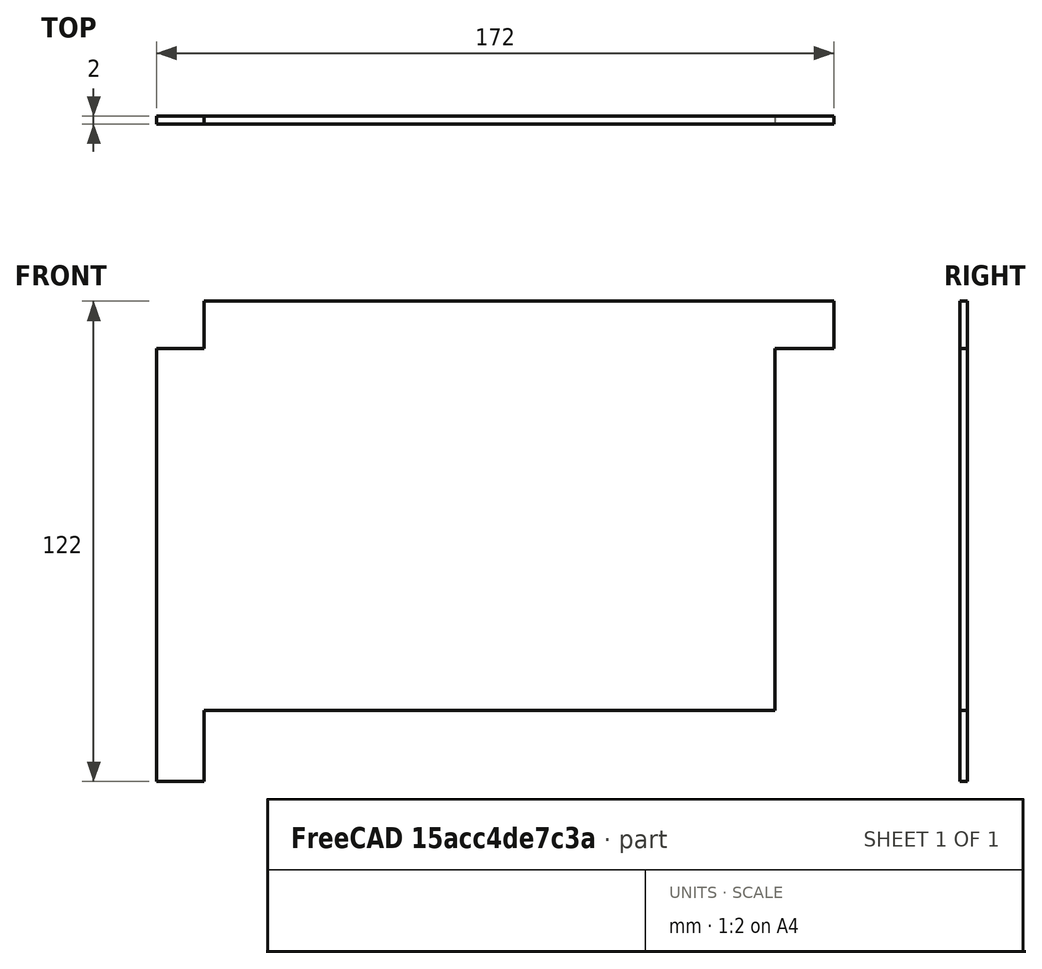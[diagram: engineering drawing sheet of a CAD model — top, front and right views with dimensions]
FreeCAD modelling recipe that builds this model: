
FCSTD DOCUMENT  (FreeCAD 0.20R29177 (Git))
Label: 8000_Profile_Template_Plexi
License: All rights reserved
LicenseURL: http://en.wikipedia.org/wiki/All_rights_reserved
objects: TechDraw::DrawViewDimension×6, Sketcher::SketchObject×1, PartDesign::Pad×1, PartDesign::Body×1, TechDraw::DrawSVGTemplate×1, TechDraw::DrawViewPart×1, TechDraw::DrawPage×1
note: 4 computed .brp shape members not serialized (recipe doc carries the construction recipe); baked Part::Feature solids carry a one-line shape summary decoded from their .brp

FEATURE [Sketcher::SketchObject] Sketch
  FullyConstrained = true
  MapMode = 5
  Placement = pos=(0,0,0) rot=(1,0,0;1.5708rad)
  Support = -> [XZ_Plane]
  sketch-geometry (10):
    g0: LineSegment StartX=0 StartY=0 StartZ=0 EndX=0 EndY=110 EndZ=0
    g1: LineSegment StartX=0 StartY=0 StartZ=0 EndX=12 EndY=0 EndZ=0
    g2: LineSegment StartX=12 StartY=0 StartZ=0 EndX=12 EndY=18 EndZ=0
    g3: LineSegment StartX=12 StartY=18 StartZ=0 EndX=157 EndY=18 EndZ=0
    g4: LineSegment StartX=157 StartY=18 StartZ=0 EndX=157 EndY=110 EndZ=0
    g5: LineSegment StartX=157 StartY=110 StartZ=0 EndX=172 EndY=110 EndZ=0
    g6: LineSegment StartX=172 StartY=110 StartZ=0 EndX=172 EndY=122 EndZ=0
    g7: LineSegment StartX=172 StartY=122 StartZ=0 EndX=12 EndY=122 EndZ=0
    g8: LineSegment StartX=0 StartY=110 StartZ=0 EndX=12 EndY=110 EndZ=0
    g9: LineSegment StartX=12 StartY=110 StartZ=0 EndX=12 EndY=122 EndZ=0
  constraints (30):
    c: Vertical(g0)
    c: DistanceY(g0,g0) = 110
    c: Coincident(g1,g0)
    c: Horizontal(g1)
    c: Coincident(g2,g1)
    c: Vertical(g2)
    c: Coincident(g3,g2)
    c: Horizontal(g3)
    c: Coincident(g4,g3)
    c: Vertical(g4)
    c: Coincident(g5,g4)
    c: Horizontal(g5)
    c: Coincident(g6,g5)
    c: Vertical(g6)
    c: Horizontal(g7)
    c: DistanceX(g0,g1) = 12
    c: DistanceY(g3,g4) = 92
    c: DistanceY(g1,g2) = 18
    c: Coincident(g8,g0)
    c: Horizontal(g8)
    c: Coincident(g9,g8)
    c: Coincident(g9,g7)
    c: Vertical(g9)
    c: DistanceY(g6,g6) = 12
    c: Equal(g1,g8)
    c: Horizontal(g4,g8)
    c: DistanceX(g2,g3) = 145
    c: DistanceX(g7,g6) = 160
    c: Coincident(g6,g7)
    c: Coincident(g-1,g0)
FEATURE [PartDesign::Pad] Pad
  Direction = (0,-1,-2e-16)
  Length = 2
  Length2 = 100
  Placement = pos=(0,0,0) rot=(1,0,0;1.5708rad)
  Profile = -> Sketch
  Type = 0
FEATURE [PartDesign::Body] Body
  Group = -> [Sketch,Pad]
  Origin = -> Origin
  Tip = -> Pad
FEATURE [TechDraw::DrawSVGTemplate] Template
  EditableTexts = Designed_by_Name=RIP; Drawing_number=8000_Profile_Template; FC-Date=Date; FC-SC=1:1; FC-SH=Sheet; FC-Title=Keyboard Template; Subtitle=Printable; Weight=-
  Height = 210
  Orientation = 1
  Width = 297
FEATURE [TechDraw::DrawViewPart] View
  CoarseView = false
  Direction = (0,-1,0)
  Focus = 100
  HardHidden = false
  IsoCount = 0
  IsoHidden = false
  IsoVisible = false
  LockPosition = false
  Perspective = false
  Rotation = 0
  ScaleType = 0
  SeamHidden = false
  SeamVisible = true
  SmoothHidden = false
  SmoothVisible = true
  Source = -> [Template,Pad]
  X = 125.167
  XDirection = (0.866,0.5,0)
  Y = 122.642
FEATURE [TechDraw::DrawViewDimension] Dimension
  AngleOverride = false
  Arbitrary = false
  ArbitraryTolerances = false
  EqualTolerance = true
  ExtensionAngle = 0
  FormatSpec = %.2f
  FormatSpecOverTolerance = %+.2f
  FormatSpecUnderTolerance = %+.2f
  Inverted = false
  LineAngle = 0
  LockPosition = false
  MeasureType = 1
  OverTolerance = 0
  References2D = -> [View]
  Rotation = 0
  ScaleType = 0
  TheoreticalExact = false
  Type = 2
  UnderTolerance = 0
  X = 109.768
  Y = 55
FEATURE [TechDraw::DrawViewDimension] Dimension001
  AngleOverride = false
  Arbitrary = false
  ArbitraryTolerances = false
  EqualTolerance = true
  ExtensionAngle = 0
  FormatSpec = %.2f
  FormatSpecOverTolerance = %+.2f
  FormatSpecUnderTolerance = %+.2f
  Inverted = false
  LineAngle = 0
  LockPosition = false
  MeasureType = 1
  OverTolerance = 0
  References2D = -> [View]
  Rotation = 0
  ScaleType = 0
  TheoreticalExact = false
  Type = 2
  UnderTolerance = 0
  X = 95.3726
  Y = 3.43089
FEATURE [TechDraw::DrawViewDimension] Dimension003
  AngleOverride = false
  Arbitrary = false
  ArbitraryTolerances = false
  EqualTolerance = true
  ExtensionAngle = 0
  FormatSpec = %.2f
  FormatSpecOverTolerance = %+.2f
  FormatSpecUnderTolerance = %+.2f
  Inverted = false
  LineAngle = 0
  LockPosition = false
  MeasureType = 1
  OverTolerance = 0
  References2D = -> [View]
  Rotation = 0
  ScaleType = 0
  TheoreticalExact = false
  Type = 1
  UnderTolerance = 0
  X = -82.4267
  Y = -79.7805
FEATURE [TechDraw::DrawViewDimension] Dimension004
  AngleOverride = false
  Arbitrary = false
  ArbitraryTolerances = false
  EqualTolerance = true
  ExtensionAngle = 0
  FormatSpec = %.2f
  FormatSpecOverTolerance = %+.2f
  FormatSpecUnderTolerance = %+.2f
  Inverted = false
  LineAngle = 0
  LockPosition = false
  MeasureType = 1
  OverTolerance = 0
  References2D = -> [View]
  Rotation = 0
  ScaleType = 0
  TheoreticalExact = false
  Type = 2
  UnderTolerance = 0
  X = -105.784
  Y = -3.15447
FEATURE [TechDraw::DrawViewDimension] Dimension005
  AngleOverride = false
  Arbitrary = false
  ArbitraryTolerances = false
  EqualTolerance = true
  ExtensionAngle = 0
  FormatSpec = %.2f
  FormatSpecOverTolerance = %+.2f
  FormatSpecUnderTolerance = %+.2f
  Inverted = false
  LineAngle = 0
  LockPosition = false
  MeasureType = 1
  OverTolerance = 0
  References2D = -> [View]
  Rotation = 0
  ScaleType = 0
  TheoreticalExact = false
  Type = 1
  UnderTolerance = 0
  X = -10.0189
  Y = -45.8374
FEATURE [TechDraw::DrawViewDimension] Dimension006
  AngleOverride = false
  Arbitrary = false
  ArbitraryTolerances = false
  EqualTolerance = true
  ExtensionAngle = 0
  FormatSpec = %.2f
  FormatSpecOverTolerance = %+.2f
  FormatSpecUnderTolerance = %+.2f
  Inverted = false
  LineAngle = 0
  LockPosition = false
  MeasureType = 1
  OverTolerance = 0
  References2D = -> [View]
  Rotation = 0
  ScaleType = 0
  TheoreticalExact = false
  Type = 1
  UnderTolerance = 0
  X = 7.42276
  Y = 74.374
FEATURE [TechDraw::DrawPage] Page
  KeepUpdated = true
  NextBalloonIndex = 1
  ProjectionType = 0
  Template = -> Template
  Views = -> [View,Dimension,Dimension001,Dimension003,Dimension004,Dimension005,Dimension006]
